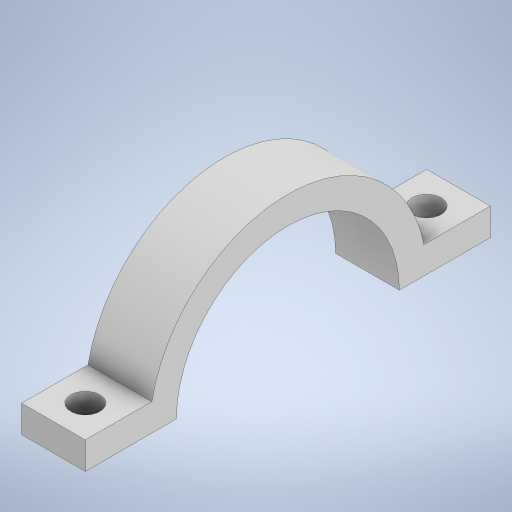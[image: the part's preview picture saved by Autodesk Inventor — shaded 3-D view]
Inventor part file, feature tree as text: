
AUTODESK INVENTOR PART (.ipt)
format: ipt  version: 2023 (Build 270158000, 158)  size: 261,632 bytes
history: native  units: mm
features: sketch x3, extrude x2, hole x1, mirror x1
ambient origin geometry x8: Origin, YZ Plane, XZ Plane, XY Plane, X Axis, Y Axis, Z Axis, Center Point
bodies: Volumenkörper1 (feature_tree)
feature tree (7):
  extrude  "Extrusion1"  TaperAngle=180.0deg  [1 undecoded]
  extrude  "Extrusion3"  Depth=7.0mm TaperAngle=0.0deg
  hole  "Bohrung1"  [1 undecoded]
  mirror  "Spiegeln1"
  sketch  "Skizze1"  dims[d0=12.25mm d1=180.0deg]
  sketch  "Skizze3"  dims[d3=15.25mm d4=7.0mm d5=0.0mm]
  sketch  "Skizze5"  dims[d6=7.0mm d7=3.0mm d10=7.0mm d11=0.0mm d12=3.2mm d13=6.0mm d14=4.0mm d15=2.0mm d16=90.0deg d17=8.0mm d18=20.594885mm d19=3.5mm d20=3.5mm]
note: 2 required parameter values undecoded (feature->parameter linkage not recoverable at this tier; creation-order binding heuristic only, values carry confidence <= 0.55)
